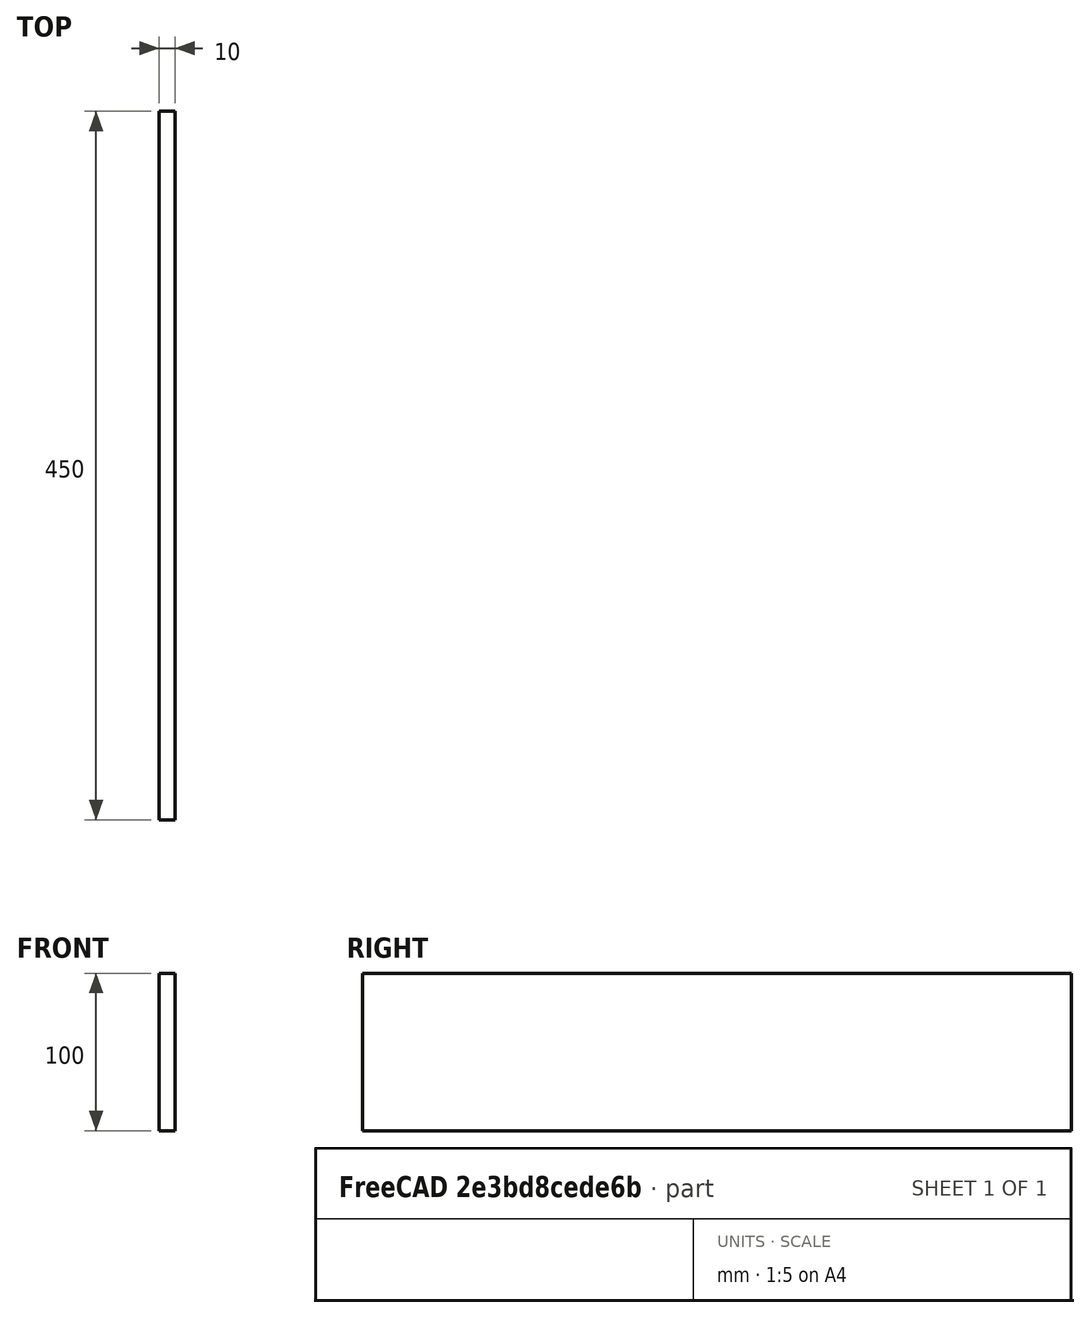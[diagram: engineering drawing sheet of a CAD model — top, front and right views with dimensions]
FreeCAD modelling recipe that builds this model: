
FCSTD DOCUMENT  (FreeCAD 0.20R29603 (Git))
Label: 500_Back_Horizontal_Top
License: All rights reserved
LicenseURL: http://en.wikipedia.org/wiki/All_rights_reserved
objects: Sketcher::SketchObject×1, Spreadsheet::Sheet×1, PartDesign::Pad×1, PartDesign::Body×1
note: 4 computed .brp shape members not serialized (recipe doc carries the construction recipe); baked Part::Feature solids carry a one-line shape summary decoded from their .brp

FEATURE [Sketcher::SketchObject] Sketch
  FullyConstrained = true
  MapMode = 4
  Placement = pos=(0,0,0) rot=(0.57735,0.57735,0.57735;2.0944rad)
  Support = -> [XY_Plane]
  expr: Constraints[5] = Spreadsheet.nZ
  expr: Constraints[6] = Spreadsheet.nY
  sketch-geometry (5):
    g0: LineSegment StartX=0 StartY=0 StartZ=0 EndX=0 EndY=100 EndZ=0
    g1: LineSegment StartX=450 StartY=0 StartZ=0 EndX=450 EndY=100 EndZ=0
    g2: LineSegment StartX=450 StartY=100 StartZ=0 EndX=0 EndY=100 EndZ=0
    g3: LineSegment StartX=225 StartY=0 StartZ=0 EndX=0 EndY=0 EndZ=0
    g4: LineSegment StartX=450 StartY=0 StartZ=0 EndX=225 EndY=0 EndZ=0
  constraints (14):
    c: Vertical(g0)
    c: Vertical(g1)
    c: Coincident(g2,g1)
    c: Coincident(g2,g0)
    c: Horizontal(g2)
    c: DistanceY(g1,g1) = 100
    c: DistanceX(g2,g2) = 450
    c: Coincident(g3,g0)
    c: Coincident(g4,g1)
    c: Horizontal(g4)
    c: Equal(g3,g4)
    c: Coincident(g4,g3)
    c: Horizontal(g3)
    c: Coincident(g0,g-1)
FEATURE [Spreadsheet::Sheet] Spreadsheet  label="xls"
  cells = B7=KEYBOARD FRONT; B8=Width; C8=nY; D8(nY)=450; B9=Height; C9=nZ; D9(nZ)=100; E9=F(T); B10=Thickness; C10=nT; D10(nT)=10
FEATURE [PartDesign::Pad] Pad
  AllowMultiFace = false
  Direction = (1,0,0)
  Length = 10
  Length2 = 100
  Profile = -> Sketch
  Reversed = true
  Type = 0
  expr: Length = Spreadsheet.nT
FEATURE [PartDesign::Body] Body
  Group = -> [Sketch,Pad]
  Origin = -> Origin
  Tip = -> Pad
